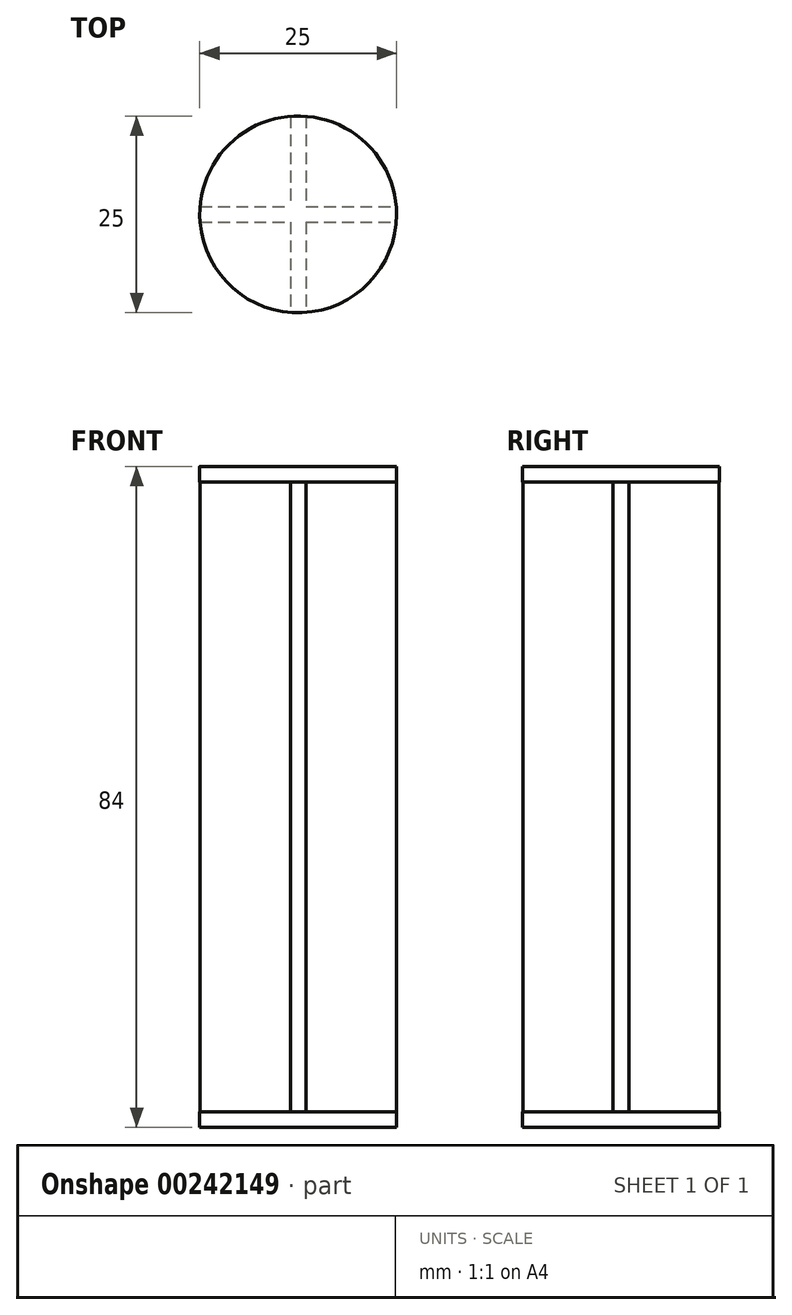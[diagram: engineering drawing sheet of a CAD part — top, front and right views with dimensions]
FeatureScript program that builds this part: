
annotation { "Feature Type Name" : "Feature", "Feature Type Description" : "" }
export const myFeature = defineFeature(function(context is Context, id is Id, definition is map)
    precondition{}
    {
        {
            var Q0;
            Q0=qCreatedBy(makeId("Top.planeOp"),FACE);
            var sketch = newSketch(context, id + "F0", { "sketchPlane" : qUnion([Q0])});
            skCircle(sketch, "E0", {"center": v(0, 0) * mm, "radius": 12.5 * mm});
            skSolve(sketch);
        }
        {
            var Q0;
            Q0 = qSketchRegion(id + "F0", true);
            extrude(context, id + "F1", {"entities" : qUnion([Q0]), "depth" : 2 * mm});
        }
        {
            var Q0;
            Q0=makeQuery(id+"F1.opExtrude","CAP_FACE",FACE,{"disambiguationData":[OSD([sQuery(id+"F0.wireOp",EDGE,"E0")])],"isStart":false});
            var sketch = newSketch(context, id + "F2", { "sketchPlane" : qUnion([Q0])});
            skLineSegment(sketch, "E1.bottom", {"start": v(-1, 12.46) * mm, "end": v(1, 12.46) * mm});
            skLineSegment(sketch, "E1.top", {"start": v(-1, -12.46) * mm, "end": v(1, -12.46) * mm});
            skLineSegment(sketch, "E1.left", {"start": v(-1, 12.46) * mm, "end": v(-1, -12.46) * mm});
            skLineSegment(sketch, "E1.right", {"start": v(1, 12.46) * mm, "end": v(1, -12.46) * mm});
            skLineSegment(sketch, "E2.bottom", {"start": v(-12.46, 1) * mm, "end": v(12.46, 1) * mm});
            skLineSegment(sketch, "E2.top", {"start": v(-12.46, -1) * mm, "end": v(12.46, -1) * mm});
            skLineSegment(sketch, "E2.left", {"start": v(-12.46, 1) * mm, "end": v(-12.46, -1) * mm});
            skLineSegment(sketch, "E2.right", {"start": v(12.46, 1) * mm, "end": v(12.46, -1) * mm});
            skSolve(sketch);
        }
        {
            var Q0;
            Q0 = qSketchRegion(id + "F2", true);
            extrude(context, id + "F3", {"entities" : qUnion([Q0]), "operationType" : NewBodyOperationType.ADD, "depth" : 80 * mm});
        }
        {
            var Q0;
            Q0=makeQuery(id+"F3.opExtrude","CAP_FACE",FACE,{"disambiguationData":[OSD([sQuery(id+"F2.wireOp",EDGE,"E1.bottom"),sQuery(id+"F2.wireOp",EDGE,"E1.top"),sQuery(id+"F2.wireOp",EDGE,"E1.left"),sQuery(id+"F2.wireOp",EDGE,"E1.right"),sQuery(id+"F2.wireOp",EDGE,"E2.bottom"),sQuery(id+"F2.wireOp",EDGE,"E2.top"),sQuery(id+"F2.wireOp",EDGE,"E2.left"),sQuery(id+"F2.wireOp",EDGE,"E2.right")])],"isStart":false});
            var sketch = newSketch(context, id + "F4", { "sketchPlane" : qUnion([Q0])});
            skCircle(sketch, "E3", {"center": v(0, 0) * mm, "radius": 12.5 * mm});
            skSolve(sketch);
        }
        {
            var Q0;
            Q0 = qSketchRegion(id + "F4", true);
            extrude(context, id + "F5", {"entities" : qUnion([Q0]), "operationType" : NewBodyOperationType.ADD, "depth" : 2 * mm});
        }
    });
